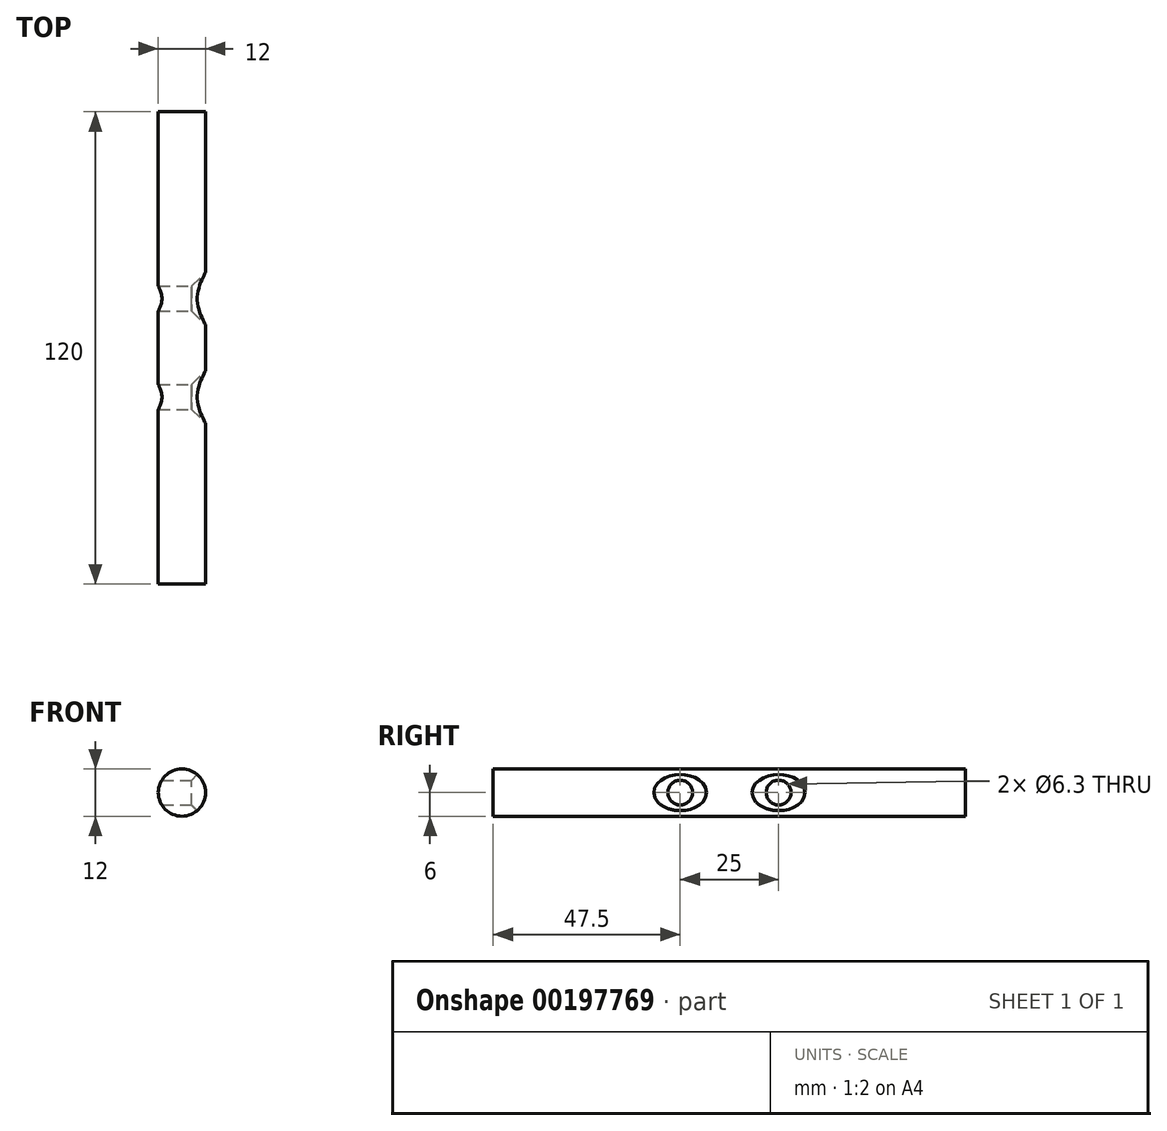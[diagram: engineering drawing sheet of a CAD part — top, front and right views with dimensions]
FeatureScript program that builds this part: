
annotation { "Feature Type Name" : "Feature", "Feature Type Description" : "" }
export const myFeature = defineFeature(function(context is Context, id is Id, definition is map)
    precondition{}
    {
        {
            var Q0;
            Q0=qCreatedBy(makeId("Front.planeOp"),FACE);
            var sketch = newSketch(context, id + "F0", { "sketchPlane" : qUnion([Q0])});
            skCircle(sketch, "E0", {"center": v(-6, 0) * mm, "radius": 6 * mm});
            skSolve(sketch);
        }
        {
            var Q0;
            Q0 = qSketchRegion(id + "F0", true);
            extrude(context, id + "F1", {"entities" : qUnion([Q0]), "endBound" : BoundingType.SYMMETRIC, "depth" : 120 * mm});
        }
        {
            var Q0;
            Q0=qCreatedBy(makeId("Right.planeOp"),FACE);
            var sketch = newSketch(context, id + "F2", { "sketchPlane" : qUnion([Q0])});
            skCircle(sketch, "E1", {"center": v(-12.5, 0) * mm, "radius": 3 * mm});
            skCircle(sketch, "E2", {"center": v(12.5, 0) * mm, "radius": 3 * mm});
            skSolve(sketch);
        }
        {
            var Q0;
            Q0=sQuery(id+"F2.wireOp",VERTEX,"E2.center");
            var Q1;
            Q1=sQuery(id+"F2.wireOp",VERTEX,"E1.center");
            var Q2;
            Q2=makeQuery(id+"F1.opExtrude","SWEPT_BODY",BODY,{"disambiguationData":[OSD([sQuery(id+"F0.wireOp",EDGE,"E0")])]});
            hole(context, id + "F3", {"style" : HoleStyle.C_SINK, "endStyle" : HoleEndStyle.THROUGH, "standardTappedOrClearance" : lookupTablePath({ "standard" : "ISO", "fit" : "Close", "size" : "M6", "type" : "Clearance" }), "standardBlindInLast" : lookupTablePath({ "fit" : "Close", "standard" : "ISO", "size" : "M6", "type" : "Clearance" }), "holeDiameter" : 6.3 * mm, "cSinkDiameter" : 13.44 * mm, "cSinkAngle" : 90 * degree, "locations" : qUnion([Q0, Q1]), "scope" : qUnion([Q2]), "isTappedThrough" : true});
        }
    });
